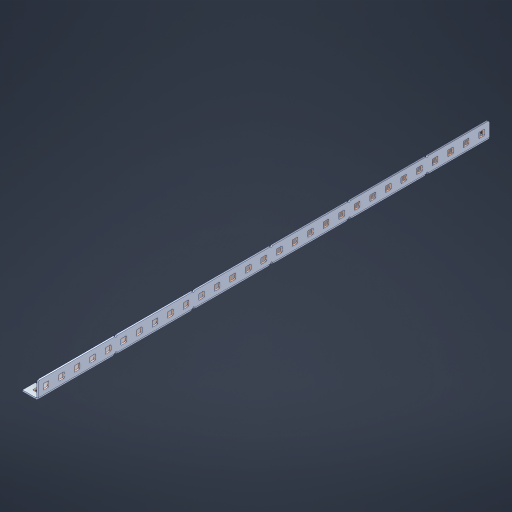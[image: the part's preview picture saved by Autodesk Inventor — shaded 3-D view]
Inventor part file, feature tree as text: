
AUTODESK INVENTOR PART (.ipt)
format: ipt  version: 2023 (Build 270158000, 158)  size: 1,172,992 bytes
history: native  units: in
note: dims shown in document units (in); Inventor stores cm internally (conversion verified against a paired STEP export)
features: other x94, extrude x85, sheet_metal_op x11, sketch x10, pattern_linear x2, mirror x1, chamfer x1
ambient origin geometry x8: Origin, YZ Plane, XZ Plane, XY Plane, X Axis, Y Axis, Z Axis, Center Point
bodies: Solid1 (feature_tree), Body (feature_tree)
feature tree (204):
  sheet_metal_op  "Flanges"
  other  "Flange Pattern Plane"
  other  "Flange Pattern Sketch"
  sheet_metal_op  "Flange Pattern"
  sheet_metal_op  "Body Pattern"
  pattern_linear  "Center Pattern"  Spacing1=0.0469in  [1 undecoded]
  other  "Arc Length"
  mirror  "Notch Mirror"
  pattern_linear  "Notch Pattern"  Spacing1=0.182in  [1 undecoded]
  chamfer  "End Chamfer"
  extrude  "Half Cut"  Depth=0.02in
  sketch  "Sketch1"  dims[d0=1.0in]
  other  "Plate1"
  sketch  "Sketch2"  dims[d1=14.5in]
  other  "Plate2"
  sheet_metal_op  "Bend1"
  sheet_metal_op  "Corner1"
  sketch  "Sketch3"  dims[d2=0.0469in]
  sketch  "Sketch7"  dims[d3=0.0469in]
  other  "Srf1"
  other  "Srf2"
  sketch  "Sketch8"  dims[d4=0.0234in]
  sketch  "Sketch9"  dims[d5=0.0938in]
  other  "Srf91"
  sheet_metal_op  "Body Pattern Sketch"
  other  "Srf92"
  sketch  "Sketch13"  dims[d6=0.0469in]
  sketch  "Sketch14"  dims[d7=0.5in d8=90.0deg d9=0.0312in]
  sketch  "Sketch15"  dims[d10=0.1875in]
  sketch  "Sketch16"  dims[d11=0.0469in d12=0.0469in d16=0.182in d17=0.02in d18=0.0469in d19=0.0in d20=0.25in d21=0.25in d38=11.4173in d40=0.5in d41=0.3937in d43=1.0in d46=0.172in d47=1.0in d48=0.0in d49=0.182in d50=0.02in d51=0.25in d52=0.25in d53=0.0469in d54=0.0in d55=0.172in d56=1.0in d57=0.0in d58=0.25in d60=11.4173in d62=0.5in d63=0.3937in d65=0.5in d85=0.1227in d86=0.1659in d88=0.04in d89=0.0469in d90=0.0in d91=0.04in d92=0.0491in d95=2.5in d96=0.04in d97=0.25in d98=45.0deg d99=0.25in d100=0.5in d101=0.0in d102=2.497in d106=0.182in d107=0.02in d108=0.5in d109=0.5in d110=0.0469in d111=0.0in d112=0.172in d113=0.5in d114=0.0in d117=0.5in d118=0.5in d119=0.5in]
  other  "Srf786"
  other  "Srf823"
  other  "Srf824"
  other  "Srf825"
  other  "Srf826"
  other  "Srf827"
  other  "Srf828"
  other  "Srf829"
  other  "Srf856"
  other  "Srf857"
  other  "Srf858"
  other  "Srf859"
  other  "Srf860"
  other  "Srf861"
  other  "Srf862"
  other  "Srf889"
  other  "Srf890"
  other  "Srf891"
  other  "Srf892"
  other  "Srf893"
  other  "Srf894"
  other  "Srf895"
  other  "Srf896"
  other  "Srf922"
  other  "Srf923"
  other  "Srf924"
  other  "Srf925"
  other  "Srf926"
  other  "Srf959"
  other  "Srf960"
  other  "Srf961"
  other  "Srf962"
  other  "Srf963"
  other  "Srf996"
  other  "Srf997"
  other  "Srf998"
  other  "Srf999"
  other  "Srf1000"
  other  "Srf1143"
  other  "Srf1144"
  other  "Srf1145"
  other  "Srf1146"
  other  "Srf1147"
  other  "Srf1148"
  other  "Srf1149"
  other  "Srf1150"
  other  "Srf1151"
  other  "Srf1152"
  other  "Srf1153"
  other  "Srf1154"
  other  "Srf1155"
  other  "Srf1156"
  other  "Srf1157"
  other  "Srf1199"
  other  "Srf1200"
  other  "Srf1201"
  other  "Srf1202"
  other  "Srf1203"
  other  "Srf1204"
  other  "Srf1205"
  other  "Srf1206"
  other  "Srf1207"
  other  "Srf1208"
  other  "Srf1209"
  other  "Srf1210"
  other  "Srf1211"
  other  "Srf1212"
  other  "Srf1213"
  other  "Srf1255"
  other  "Srf1256"
  other  "Srf1257"
  other  "Srf1258"
  other  "Srf1259"
  other  "Srf1260"
  other  "Srf1261"
  other  "Srf1262"
  other  "Srf1263"
  other  "Srf1264"
  other  "Srf1265"
  other  "Srf1266"
  other  "Srf1267"
  other  "Srf1268"
  other  "Srf1269"
  sheet_metal_op  "Flange Stamp"
  sheet_metal_op  "Flange Circle"
  sheet_metal_op  "Body Stamp"
  sheet_metal_op  "Body Circle"
  other  "Center Stamp"
  other  "Center Circle"
  sheet_metal_op  "Notch"
  extrude  "ExtrusionSrf2"  Depth=0.0469in
  extrude  "ExtrusionSrf92"  TaperAngle=0.0deg  [1 undecoded]
  extrude  "ExtrusionSrf823"  Depth=0.5in
  extrude  "ExtrusionSrf824"  Depth=0.5in
  extrude  "ExtrusionSrf825"  Depth=0.5in
  extrude  "ExtrusionSrf826"  Depth=0.5in
  extrude  "ExtrusionSrf827"  Depth=1.0in TaperAngle=0.0deg
  extrude  "ExtrusionSrf828"  Depth=0.182in
  extrude  "ExtrusionSrf829"  Depth=0.02in
  extrude  "ExtrusionSrf856"  Depth=0.5in
  extrude  "ExtrusionSrf857"  Depth=0.5in
  extrude  "ExtrusionSrf858"  Depth=0.0469in
  extrude  "ExtrusionSrf859"  TaperAngle=0.0deg  [1 undecoded]
  extrude  "ExtrusionSrf860"  Depth=0.5in
  extrude  "ExtrusionSrf861"  Depth=1.0in TaperAngle=0.0deg
  extrude  "ExtrusionSrf862"  Depth=0.5in
  extrude  "ExtrusionSrf889"  Depth=0.5in
  extrude  "ExtrusionSrf890"  Depth=0.5in
  extrude  "ExtrusionSrf891"  Depth=0.5in
  extrude  "ExtrusionSrf892"  Depth=0.5in
  extrude  "ExtrusionSrf893"  Depth=0.5in
  extrude  "ExtrusionSrf894"  Depth=0.0469in
  extrude  "ExtrusionSrf895"  TaperAngle=0.0deg  [1 undecoded]
  extrude  "ExtrusionSrf896"  Depth=0.5in
  extrude  "ExtrusionSrf922"  Depth=0.5in
  extrude  "ExtrusionSrf923"  Depth=0.5in
  extrude  "ExtrusionSrf924"  Depth=0.5in TaperAngle=45.0deg
  extrude  "ExtrusionSrf925"  Depth=0.5in
  extrude  "ExtrusionSrf926"  Depth=0.5in TaperAngle=0.0deg
  extrude  "ExtrusionSrf959"  Depth=0.5in
  extrude  "ExtrusionSrf960"  Depth=0.182in
  extrude  "ExtrusionSrf961"  Depth=0.02in
  extrude  "ExtrusionSrf962"  Depth=0.5in
  extrude  "ExtrusionSrf963"  Depth=0.5in
  extrude  "ExtrusionSrf996"  Depth=0.0469in
  extrude  "ExtrusionSrf997"  TaperAngle=0.0deg  [1 undecoded]
  extrude  "ExtrusionSrf998"  Depth=0.5in
  extrude  "ExtrusionSrf999"  Depth=0.5in TaperAngle=0.0deg
  extrude  "ExtrusionSrf1000"  Depth=0.5in
  extrude  "ExtrusionSrf1143"  Depth=0.5in
  extrude  "ExtrusionSrf1144"  Depth=0.5in
  extrude  "ExtrusionSrf1145"  [1 undecoded]
  extrude  "ExtrusionSrf1146"  [1 undecoded]
  extrude  "ExtrusionSrf1147"  [1 undecoded]
  extrude  "ExtrusionSrf1148"  [1 undecoded]
  extrude  "ExtrusionSrf1149"  [1 undecoded]
  extrude  "ExtrusionSrf1150"  [1 undecoded]
  extrude  "ExtrusionSrf1151"  [1 undecoded]
  extrude  "ExtrusionSrf1152"  [1 undecoded]
  extrude  "ExtrusionSrf1153"  [1 undecoded]
  extrude  "ExtrusionSrf1154"  [1 undecoded]
  extrude  "ExtrusionSrf1155"  [1 undecoded]
  extrude  "ExtrusionSrf1156"  [1 undecoded]
  extrude  "ExtrusionSrf1157"  [1 undecoded]
  extrude  "ExtrusionSrf1199"  [1 undecoded]
  extrude  "ExtrusionSrf1200"  [1 undecoded]
  extrude  "ExtrusionSrf1201"  [1 undecoded]
  extrude  "ExtrusionSrf1202"  [1 undecoded]
  extrude  "ExtrusionSrf1203"  [1 undecoded]
  extrude  "ExtrusionSrf1204"  [1 undecoded]
  extrude  "ExtrusionSrf1205"  [1 undecoded]
  extrude  "ExtrusionSrf1206"  [1 undecoded]
  extrude  "ExtrusionSrf1207"  [1 undecoded]
  extrude  "ExtrusionSrf1208"  [1 undecoded]
  extrude  "ExtrusionSrf1209"  [1 undecoded]
  extrude  "ExtrusionSrf1210"  [1 undecoded]
  extrude  "ExtrusionSrf1211"  [1 undecoded]
  extrude  "ExtrusionSrf1212"  [1 undecoded]
  extrude  "ExtrusionSrf1213"  [1 undecoded]
  extrude  "ExtrusionSrf1255"  [1 undecoded]
  extrude  "ExtrusionSrf1256"  [1 undecoded]
  extrude  "ExtrusionSrf1257"  [1 undecoded]
  extrude  "ExtrusionSrf1258"  [1 undecoded]
  extrude  "ExtrusionSrf1259"  [1 undecoded]
  extrude  "ExtrusionSrf1260"  [1 undecoded]
  extrude  "ExtrusionSrf1261"  [1 undecoded]
  extrude  "ExtrusionSrf1262"  [1 undecoded]
  extrude  "ExtrusionSrf1263"  [1 undecoded]
  extrude  "ExtrusionSrf1264"  [1 undecoded]
  extrude  "ExtrusionSrf1265"  [1 undecoded]
  extrude  "ExtrusionSrf1266"  [1 undecoded]
  extrude  "ExtrusionSrf1267"  [1 undecoded]
  extrude  "ExtrusionSrf1268"  [1 undecoded]
  extrude  "ExtrusionSrf1269"  [1 undecoded]
note: 49 required parameter values undecoded (feature->parameter linkage not recoverable at this tier; creation-order binding heuristic only, values carry confidence <= 0.55)
